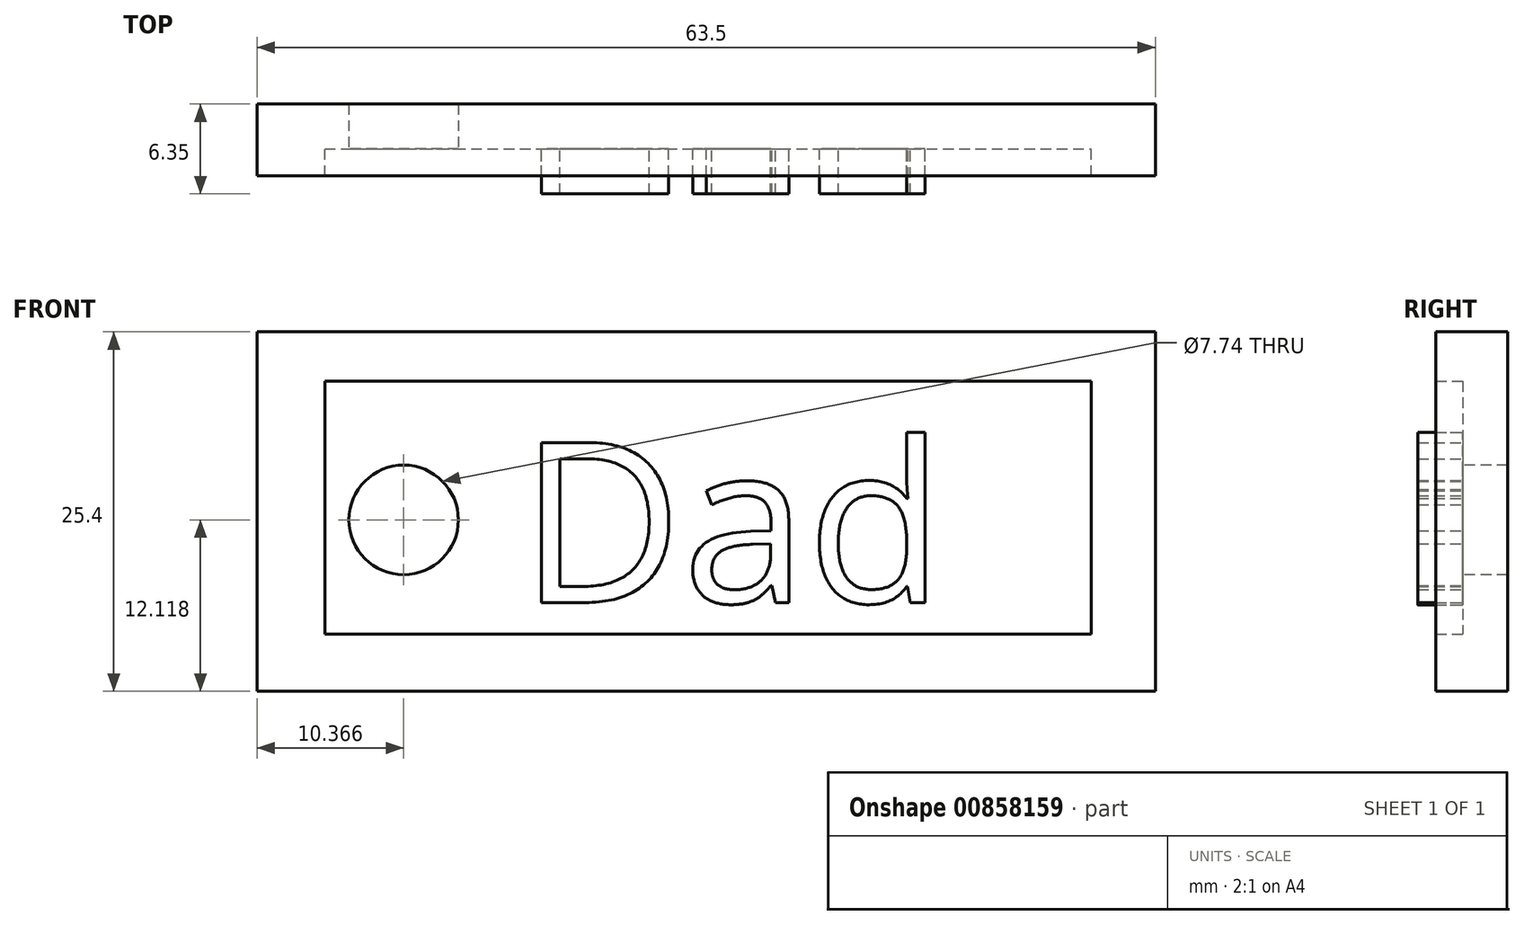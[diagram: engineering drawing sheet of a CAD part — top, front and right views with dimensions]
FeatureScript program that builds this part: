
annotation { "Feature Type Name" : "Feature", "Feature Type Description" : "" }
export const myFeature = defineFeature(function(context is Context, id is Id, definition is map)
    precondition{}
    {
        {
            var Q0;
            Q0=qCreatedBy(makeId("Front.planeOp"),FACE);
            var sketch = newSketch(context, id + "F0", { "sketchPlane" : qUnion([Q0])});
            skLineSegment(sketch, "E0.bottom", {"start": v(0, 25.4) * mm, "end": v(63.5, 25.4) * mm});
            skLineSegment(sketch, "E0.top", {"start": v(0, 0) * mm, "end": v(63.5, 0) * mm});
            skLineSegment(sketch, "E0.left", {"start": v(0, 25.4) * mm, "end": v(0, 0) * mm});
            skLineSegment(sketch, "E0.right", {"start": v(63.5, 25.4) * mm, "end": v(63.5, 0) * mm});
            skLineSegment(sketch, "E1.bottom", {"start": v(4.79, 21.92) * mm, "end": v(58.96, 21.92) * mm});
            skLineSegment(sketch, "E1.top", {"start": v(4.79, 4.05) * mm, "end": v(58.96, 4.05) * mm});
            skLineSegment(sketch, "E1.left", {"start": v(4.79, 21.92) * mm, "end": v(4.79, 4.05) * mm});
            skLineSegment(sketch, "E1.right", {"start": v(58.96, 21.92) * mm, "end": v(58.96, 4.05) * mm});
            skSolve(sketch);
        }
        {
            var Q0;
            Q0 = qSketchRegion(id + "F0", true);
            extrude(context, id + "F1", {"entities" : qUnion([Q0]), "depth" : 5.08 * mm, "offsetDistance" : 25.4 * mm});
        }
        {
            var Q0;
            Q0=makeQuery(id+"F0.imprint","IMPRINT",FACE,{"disambiguationData":[TD([[makeQuery(id+"F0.imprint","IMPRINT",EDGE,{"derivedFrom":sQuery(id+"F0.wireOp",EDGE,"E1.bottom")}),-1.0]])]});
            extrude(context, id + "F2", {"entities" : qUnion([Q0]), "operationType" : NewBodyOperationType.ADD, "depth" : 3.17 * mm, "offsetDistance" : 25.4 * mm});
        }
        {
            var Q0;
            Q0=makeQuery(id+"F2.opExtrude","CAP_FACE",FACE,{"disambiguationData":[OSD([sQuery(id+"F0.wireOp",EDGE,"E1.bottom"),sQuery(id+"F0.wireOp",EDGE,"E1.top"),sQuery(id+"F0.wireOp",EDGE,"E1.left"),sQuery(id+"F0.wireOp",EDGE,"E1.right")])],"isStart":false});
            var sketch = newSketch(context, id + "F3", { "sketchPlane" : qUnion([Q0])});
            skCircle(sketch, "E2", {"center": v(10.37, 12.12) * mm, "radius": 3.87 * mm});
            skSolve(sketch);
        }
        {
            var Q0;
            Q0=qCreatedBy(makeId("Front.planeOp"),FACE);
            var sketch = newSketch(context, id + "F4", { "sketchPlane" : qUnion([Q0])});
            skText(sketch, "E3", { "text": "Dad", "fontName": "OpenSans-Regular.ttf"});
            const initialGuessF4  = {"E3": [0.01854, 0.00628, 1, 0, 0.01139]};
            skSetInitialGuess(sketch, initialGuessF4);
            skSolve(sketch);
        }
        {
            var Q0;
            Q0 = qSketchRegion(id + "F4", true);
            extrude(context, id + "F5", {"entities" : qUnion([Q0]), "operationType" : NewBodyOperationType.ADD, "depth" : 6.35 * mm, "offsetDistance" : 25.4 * mm});
        }
        {
            var Q0;
            Q0=makeQuery(id+"F3.imprint","IMPRINT",FACE,{"disambiguationData":[TD([[makeQuery(id+"F3.imprint","IMPRINT",EDGE,{"derivedFrom":sQuery(id+"F3.wireOp",EDGE,"E2")}),1.0]])]});
            extrude(context, id + "F6", {"entities" : qUnion([Q0]), "operationType" : NewBodyOperationType.REMOVE, "oppositeDirection" : true, "depth" : 25.4 * mm, "offsetDistance" : 25.4 * mm});
        }
    });
